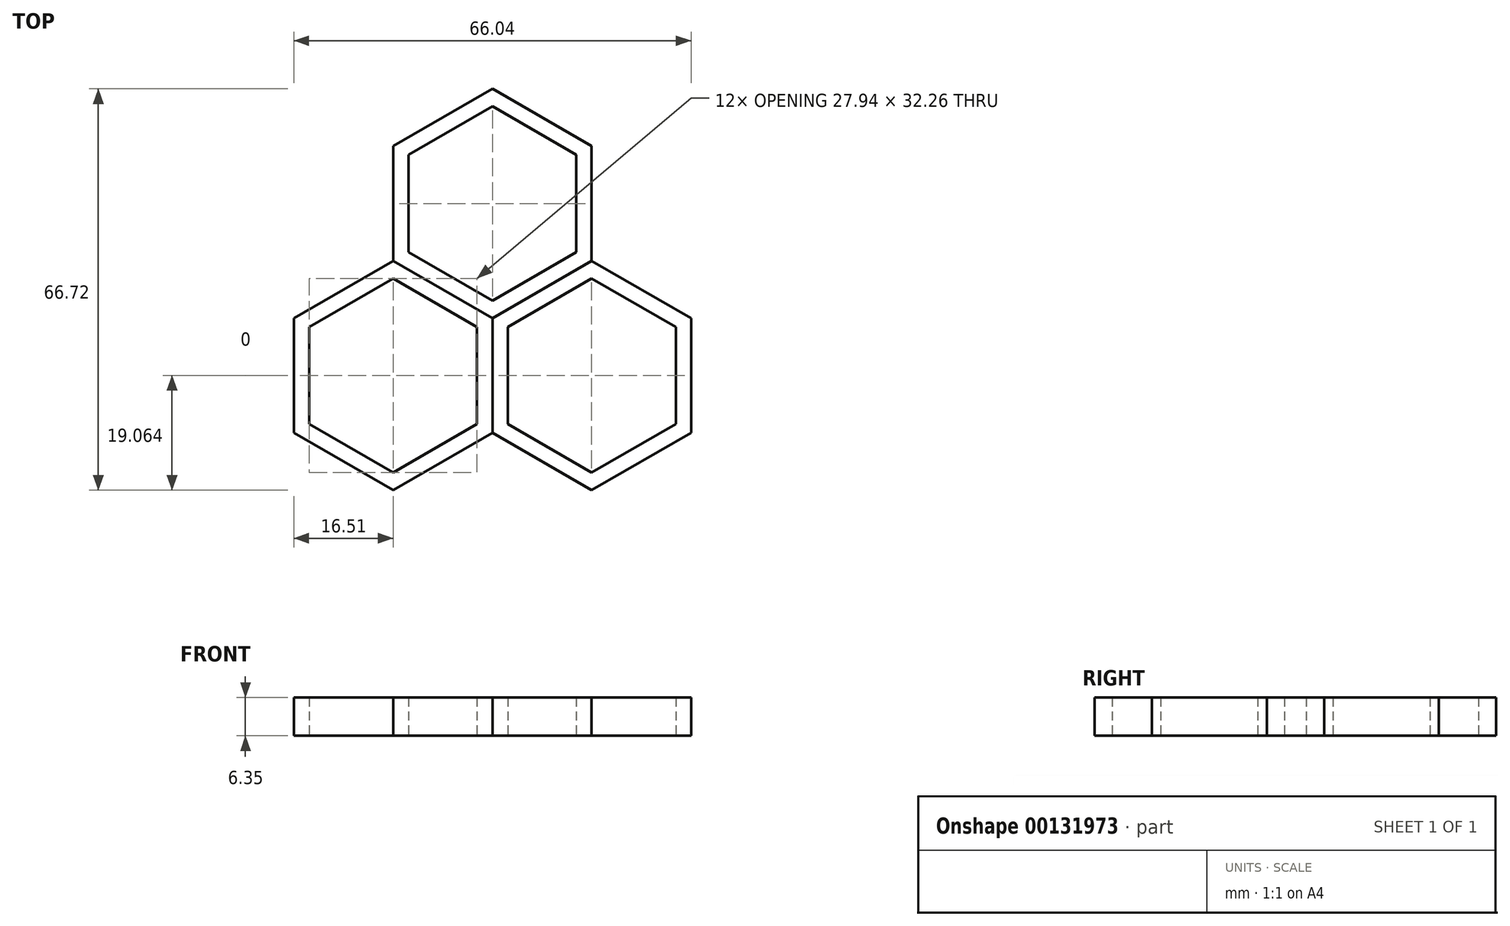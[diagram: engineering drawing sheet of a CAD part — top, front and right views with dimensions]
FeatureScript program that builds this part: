
annotation { "Feature Type Name" : "Feature", "Feature Type Description" : "" }
export const myFeature = defineFeature(function(context is Context, id is Id, definition is map)
    precondition{}
    {
        {
            var Q0;
            Q0=qCreatedBy(makeId("Top.planeOp"),FACE);
            var sketch = newSketch(context, id + "F0", { "sketchPlane" : qUnion([Q0])});
            skCircle(sketch, "E0.cCircle", {"center": v(0, 0) * mm, "radius": 16.51 * mm, "construction": true});
            skLineSegment(sketch, "E0.0", {"start": v(0, 19.06) * mm, "end": v(16.51, 9.53) * mm});
            skLineSegment(sketch, "E0.1", {"start": v(16.5, 9.53) * mm, "end": v(16.51, -9.53) * mm});
            skLineSegment(sketch, "E0.2", {"start": v(16.51, -9.53) * mm, "end": v(0, -19.06) * mm});
            skLineSegment(sketch, "E0.3", {"start": v(0, -19.06) * mm, "end": v(-16.5, -9.53) * mm});
            skLineSegment(sketch, "E0.4", {"start": v(-16.5, -9.53) * mm, "end": v(-16.51, 9.53) * mm});
            skLineSegment(sketch, "E0.5", {"start": v(-16.51, 9.53) * mm, "end": v(0, 19.06) * mm});
            skPoint(sketch, "E0.0.midPoint", {"position": v(8.25, 14.3) * mm});
            skLineSegment(sketch, "E1", {"start": v(0, -19.06) * mm, "end": v(0, 19.06) * mm, "construction": true});
            skSolve(sketch);
        }
        {
            var Q0;
            Q0=makeQuery(id+"F0.imprint","IMPRINT",FACE,{"disambiguationData":[TD([[makeQuery(id+"F0.imprint","IMPRINT",EDGE,{"derivedFrom":sQuery(id+"F0.wireOp",EDGE,"E0.0")}),-1.0]])]});
            extrude(context, id + "F1", {"entities" : qUnion([Q0]), "depth" : 6.35 * mm});
        }
        {
            var Q0;
            Q0=makeQuery(id+"F1.opExtrude","CAP_FACE",FACE,{"disambiguationData":[OSD([sQuery(id+"F0.wireOp",EDGE,"E0.0"),sQuery(id+"F0.wireOp",EDGE,"E0.1"),sQuery(id+"F0.wireOp",EDGE,"E0.2"),sQuery(id+"F0.wireOp",EDGE,"E0.3"),sQuery(id+"F0.wireOp",EDGE,"E0.4"),sQuery(id+"F0.wireOp",EDGE,"E0.5")])],"isStart":false});
            var Q1;
            Q1=makeQuery(id+"F1.opExtrude","CAP_FACE",FACE,{"disambiguationData":[OSD([sQuery(id+"F0.wireOp",EDGE,"E0.0"),sQuery(id+"F0.wireOp",EDGE,"E0.1"),sQuery(id+"F0.wireOp",EDGE,"E0.2"),sQuery(id+"F0.wireOp",EDGE,"E0.3"),sQuery(id+"F0.wireOp",EDGE,"E0.4"),sQuery(id+"F0.wireOp",EDGE,"E0.5")])],"isStart":true});
            shell(context, id + "F2", {"entities" : qUnion([Q0, Q1]), "thickness" : 2.54 * mm});
        }
        {
            var Q0;
            Q0=makeQuery(id+"F1.opExtrude","SWEPT_BODY",BODY,{"disambiguationData":[OSD([sQuery(id+"F0.wireOp",EDGE,"E0.0"),sQuery(id+"F0.wireOp",EDGE,"E0.1"),sQuery(id+"F0.wireOp",EDGE,"E0.2"),sQuery(id+"F0.wireOp",EDGE,"E0.3"),sQuery(id+"F0.wireOp",EDGE,"E0.4"),sQuery(id+"F0.wireOp",EDGE,"E0.5")])]});
            var Q1;
            Q1=makeQuery(id+"F1.opExtrude","SWEPT_EDGE",EDGE,{"disambiguationData":[OSD([sQuery(id+"F0.wireOp",EDGE,"E0.2"),sQuery(id+"F0.wireOp",EDGE,"E0.3")])]});
            circularPattern(context, id + "F3", {"entities" : qUnion([Q0]), "axis" : qUnion([Q1]), "angle" : 120 * degree, "instanceCount" : 3});
        }
    });
